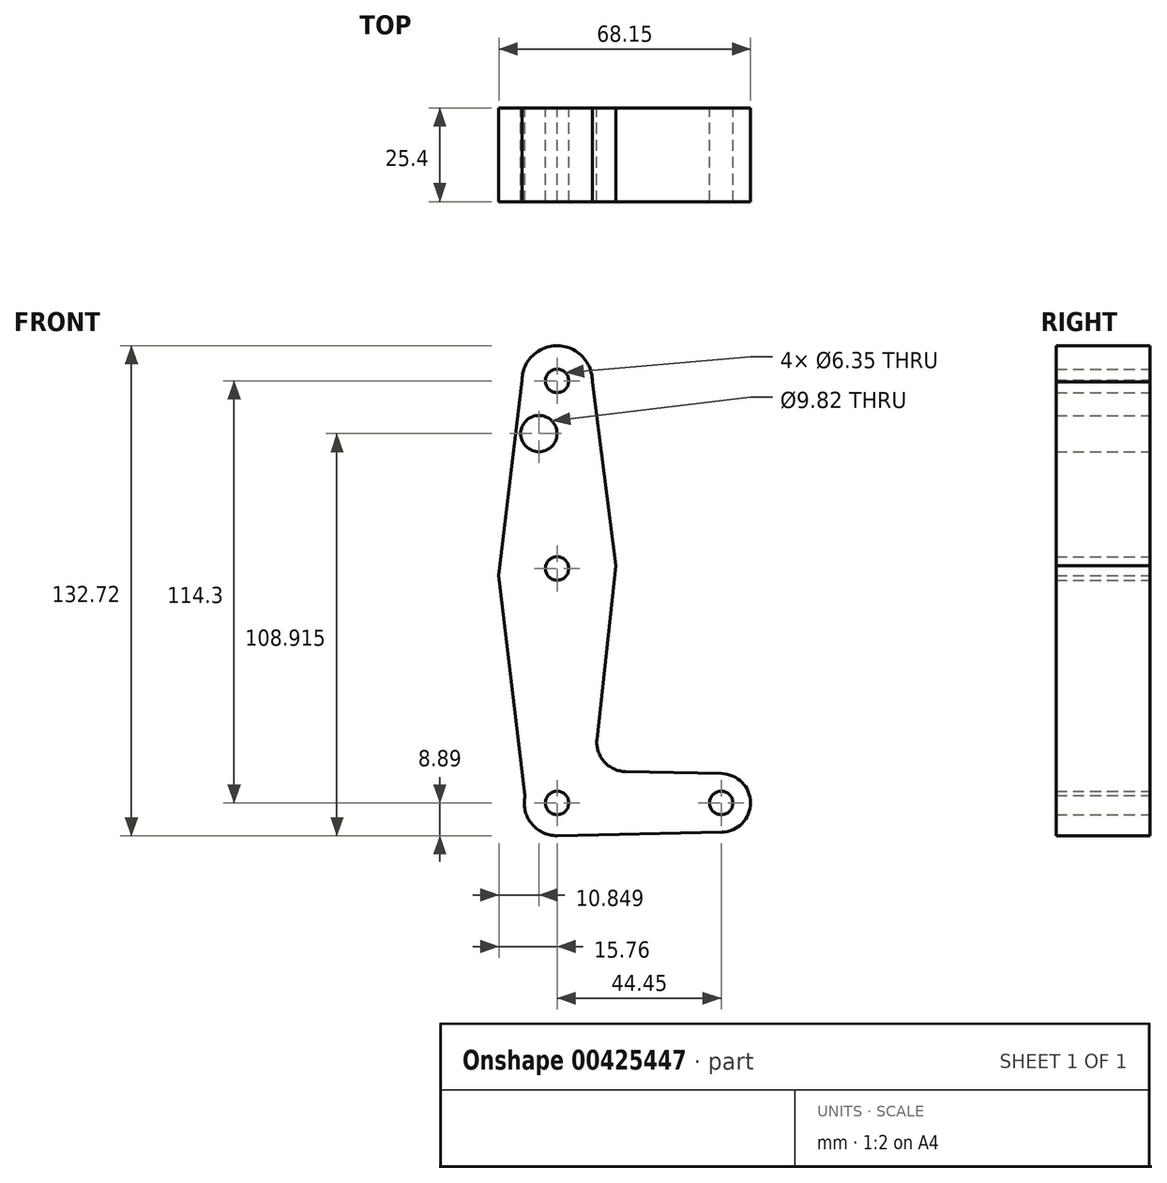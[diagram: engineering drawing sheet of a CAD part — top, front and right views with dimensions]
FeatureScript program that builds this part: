
annotation { "Feature Type Name" : "Feature", "Feature Type Description" : "" }
export const myFeature = defineFeature(function(context is Context, id is Id, definition is map)
    precondition{}
    {
        {
            var Q0;
            Q0=qCreatedBy(makeId("Front.planeOp"),FACE);
            var sketch = newSketch(context, id + "F0", { "sketchPlane" : qUnion([Q0])});
            skLineSegment(sketch, "E0", {"start": v(0, 0) * mm, "end": v(0, 114.3) * mm});
            skLineSegment(sketch, "E1", {"start": v(0, 0) * mm, "end": v(44.45, 0) * mm});
            skCircle(sketch, "E2", {"center": v(0, 114.3) * mm, "radius": 9.53 * mm});
            skCircle(sketch, "E3", {"center": v(0, 63.5) * mm, "radius": 15.88 * mm});
            skCircle(sketch, "E4", {"center": v(44.45, 0) * mm, "radius": 7.94 * mm});
            skCircle(sketch, "E5", {"center": v(0, 0) * mm, "radius": 8.9 * mm});
            skLineSegment(sketch, "E6", {"start": v(-9.52, 114.48) * mm, "end": v(-15.76, 61.62) * mm});
            skLineSegment(sketch, "E7", {"start": v(-15.76, 61.62) * mm, "end": v(-8.42, 0) * mm});
            skLineSegment(sketch, "E8", {"start": v(9.52, 114.06) * mm, "end": v(15.86, 64.25) * mm});
            skLineSegment(sketch, "E9", {"start": v(15.86, 64.25) * mm, "end": v(10.8, 17.3) * mm});
            skLineSegment(sketch, "E10", {"start": v(18.54, 8.5) * mm, "end": v(44.62, 7.94) * mm});
            skLineSegment(sketch, "E11", {"start": v(0, -8.9) * mm, "end": v(44.62, -7.94) * mm});
            skCircle(sketch, "E12", {"center": v(-4.91, 100.03) * mm, "radius": 4.91 * mm});
            skCircle(sketch, "E13", {"center": v(0, 114.3) * mm, "radius": 3.18 * mm});
            skCircle(sketch, "E14", {"center": v(0, 63.5) * mm, "radius": 3.18 * mm});
            skCircle(sketch, "E15", {"center": v(0, 0) * mm, "radius": 3.18 * mm});
            skCircle(sketch, "E16", {"center": v(44.45, 0) * mm, "radius": 3.18 * mm});
            skArc(sketch, "E17.filletArc", {"start": v(10.8, 17.3) * mm, "mid": v(12.74, 11.2) * mm, "end": v(18.54, 8.5) * mm});
            skSolve(sketch);
        }
        {
            var Q0;
            {var subQ3=sQuery(id+"F0.wireOp",EDGE,"E0");var subQ8=makeQuery(id+"F0.imprint","INTERSECT",VERTEX,{"derivedFrom":[subQ3,sQuery(id+"F0.wireOp",EDGE,"E12")]});Q0=makeQuery(id+"F0.imprint","IMPRINT",FACE,{"disambiguationData":[TD([[makeQuery(id+"F0.imprint","IMPRINT",EDGE,{"disambiguationData":[TD([[subQ8,1.0]])],"derivedFrom":subQ3}),-1.0]])]});}
            var Q1;
            {var subQ0=sQuery(id+"F0.wireOp",EDGE,"E12");Q1=makeQuery(id+"F0.imprint","IMPRINT",FACE,{"disambiguationData":[TD([[makeQuery(id+"F0.imprint","IMPRINT",EDGE,{"derivedFrom":subQ0}),-1.0]])]});}
            var Q2;
            Q2=makeQuery(id+"F0.imprint","IMPRINT",FACE,{"disambiguationData":[TD([[makeQuery(id+"F0.imprint","IMPRINT",EDGE,{"derivedFrom":sQuery(id+"F0.wireOp",EDGE,"E13")}),-1.0]])]});
            var Q3;
            {var subQ0=sQuery(id+"F0.wireOp",EDGE,"E10");Q3=makeQuery(id+"F0.imprint","IMPRINT",FACE,{"disambiguationData":[TD([[makeQuery(id+"F0.imprint","IMPRINT",EDGE,{"derivedFrom":subQ0}),-1.0]])]});}
            var Q4;
            {var subQ0=sQuery(id+"F0.wireOp",EDGE,"E5");var subQ1=sQuery(id+"F0.wireOp",EDGE,"E0");var subQ2=makeQuery(id+"F0.imprint","INTERSECT",VERTEX,{"derivedFrom":[subQ1,subQ0]});Q4=makeQuery(id+"F0.imprint","IMPRINT",FACE,{"disambiguationData":[TD([[makeQuery(id+"F0.imprint","IMPRINT",EDGE,{"disambiguationData":[TD([[subQ2,-1.0]])],"derivedFrom":subQ1}),1.0]])]});}
            var Q5;
            {var subQ0=sQuery(id+"F0.wireOp",EDGE,"E4");var subQ1=sQuery(id+"F0.wireOp",EDGE,"E1");var subQ2=makeQuery(id+"F0.imprint","INTERSECT",VERTEX,{"derivedFrom":[subQ1,subQ0]});Q5=makeQuery(id+"F0.imprint","IMPRINT",FACE,{"disambiguationData":[TD([[makeQuery(id+"F0.imprint","IMPRINT",EDGE,{"disambiguationData":[TD([[subQ2,1.0]])],"derivedFrom":subQ1}),-1.0]])]});}
            var Q6;
            Q6=makeQuery(id+"F0.imprint","IMPRINT",FACE,{"disambiguationData":[TD([[makeQuery(id+"F0.imprint","IMPRINT",EDGE,{"derivedFrom":sQuery(id+"F0.wireOp",EDGE,"E16")}),-1.0]])]});
            var Q7;
            {var subQ0=sQuery(id+"F0.wireOp",EDGE,"E15");var subQ1=sQuery(id+"F0.wireOp",EDGE,"E0");var subQ2=makeQuery(id+"F0.imprint","INTERSECT",VERTEX,{"derivedFrom":[subQ1,subQ0]});Q7=makeQuery(id+"F0.imprint","IMPRINT",FACE,{"disambiguationData":[TD([[makeQuery(id+"F0.imprint","IMPRINT",EDGE,{"disambiguationData":[TD([[subQ2,-1.0]])],"derivedFrom":subQ1}),-1.0]])]});}
            var Q8;
            {var subQ2=sQuery(id+"F0.wireOp",EDGE,"E0");var subQ4=sQuery(id+"F0.wireOp",EDGE,"E15");var subQ11=makeQuery(id+"F0.imprint","INTERSECT",VERTEX,{"derivedFrom":[subQ2,subQ4]});Q8=makeQuery(id+"F0.imprint","IMPRINT",FACE,{"disambiguationData":[TD([[makeQuery(id+"F0.imprint","IMPRINT",EDGE,{"disambiguationData":[TD([[subQ11,-1.0]])],"derivedFrom":subQ2}),1.0]])]});}
            var Q9;
            {var subQ1=sQuery(id+"F0.wireOp",EDGE,"E3");var subQ3=sQuery(id+"F0.wireOp",EDGE,"E0");var subQ8=makeQuery(id+"F0.imprint","INTERSECT",VERTEX,{"disambiguationData":[OD(0.0)],"derivedFrom":[subQ3,subQ1]});Q9=makeQuery(id+"F0.imprint","IMPRINT",FACE,{"disambiguationData":[TD([[makeQuery(id+"F0.imprint","IMPRINT",EDGE,{"disambiguationData":[TD([[subQ8,-1.0]])],"derivedFrom":subQ3}),1.0]])]});}
            var Q10;
            {var subQ1=sQuery(id+"F0.wireOp",EDGE,"E3");var subQ3=sQuery(id+"F0.wireOp",EDGE,"E0");var subQ4=makeQuery(id+"F0.imprint","INTERSECT",VERTEX,{"disambiguationData":[OD(0.0)],"derivedFrom":[subQ3,subQ1]});Q10=makeQuery(id+"F0.imprint","IMPRINT",FACE,{"disambiguationData":[TD([[makeQuery(id+"F0.imprint","IMPRINT",EDGE,{"disambiguationData":[TD([[subQ4,-1.0]])],"derivedFrom":subQ3}),-1.0]])]});}
            extrude(context, id + "F1", {"entities" : qUnion([Q0, Q1, Q2, Q3, Q4, Q5, Q6, Q7, Q8, Q9, Q10]), "depth" : 25.4 * mm});
        }
    });
